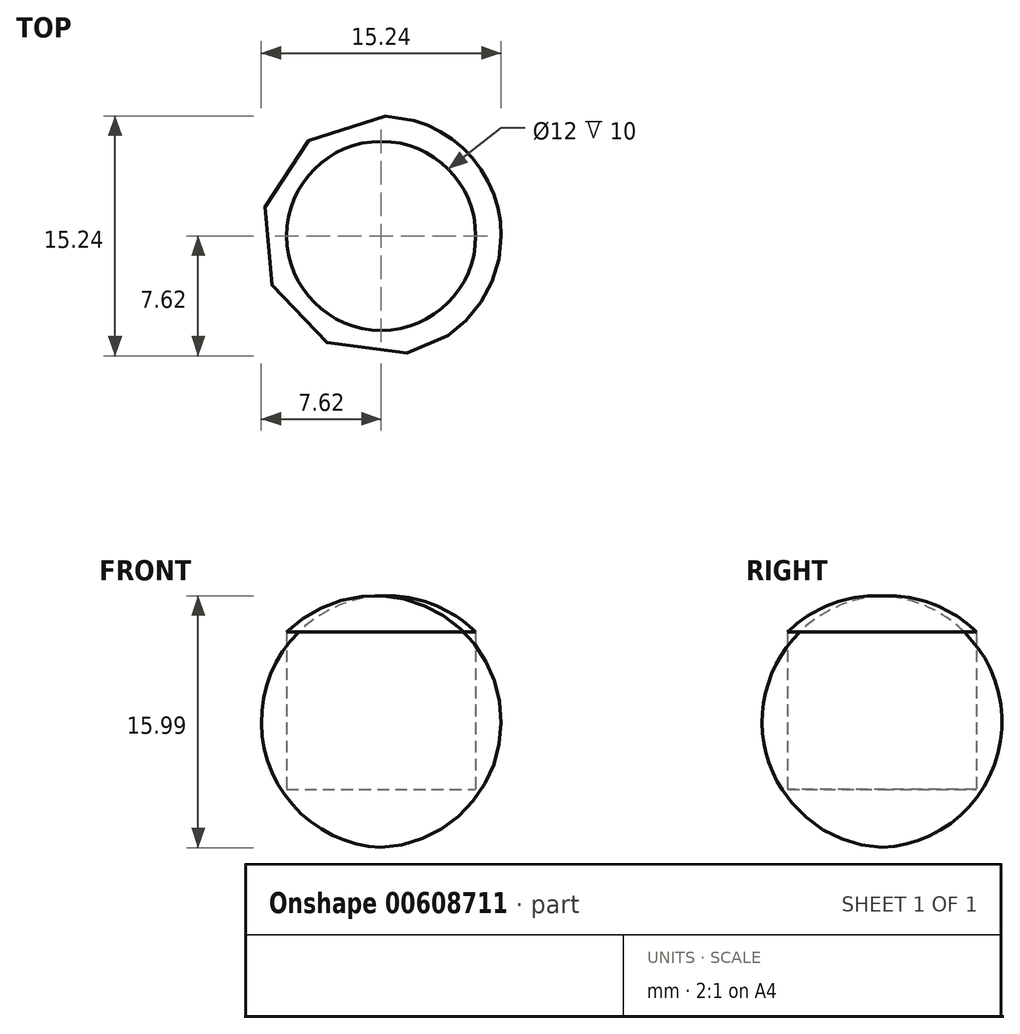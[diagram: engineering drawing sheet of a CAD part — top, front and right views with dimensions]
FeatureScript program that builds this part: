
annotation { "Feature Type Name" : "Feature", "Feature Type Description" : "" }
export const myFeature = defineFeature(function(context is Context, id is Id, definition is map)
    precondition{}
    {
        {
            var Q0;
            Q0=qCreatedBy(makeId("Front.planeOp"),FACE);
            var sketch = newSketch(context, id + "F0", { "sketchPlane" : qUnion([Q0])});
            skLineSegment(sketch, "E0", {"start": v(0, 0) * mm, "end": v(-6, 0) * mm});
            skLineSegment(sketch, "E1", {"start": v(0, 0) * mm, "end": v(0, 2.3) * mm});
            skArc(sketch, "E2", {"start": v(0, 2.3) * mm, "mid": v(-3.24, 1.78) * mm, "end": v(-6, 0) * mm});
            skSolve(sketch);
        }
        {
            var Q0;
            Q0=makeQuery(id+"F0.imprint","IMPRINT",FACE,{"disambiguationData":[TD([[makeQuery(id+"F0.imprint","IMPRINT",EDGE,{"derivedFrom":sQuery(id+"F0.wireOp",EDGE,"E0")}),-1.0]])]});
            var Q1;
            Q1=sQuery(id+"F0.wireOp",EDGE,"E1");
            revolve(context, id + "F1", {"entities" : qUnion([Q0]), "axis" : qUnion([Q1]), "revolveType" : RevolveType.FULL});
        }
        {
            var Q0;
            Q0=qCreatedBy(makeId("Front.planeOp"),FACE);
            var sketch = newSketch(context, id + "F2", { "sketchPlane" : qUnion([Q0])});
            skLineSegment(sketch, "E3.bottom", {"start": v(6, 0) * mm, "end": v(-6, 0) * mm});
            skLineSegment(sketch, "E3.top", {"start": v(6, -10) * mm, "end": v(-6, -10) * mm});
            skLineSegment(sketch, "E3.left", {"start": v(6, 0) * mm, "end": v(6, -10) * mm});
            skLineSegment(sketch, "E3.right", {"start": v(-6, 0) * mm, "end": v(-6, -10) * mm});
            skPoint(sketch, "E3.middle", {"position": v(0, -5) * mm});
            skLineSegment(sketch, "E4", {"start": v(0, -10) * mm, "end": v(0, 0) * mm});
            skSolve(sketch);
        }
        {
            var Q0;
            {var subQ0=sQuery(id+"F2.wireOp",EDGE,"E3.right");Q0=makeQuery(id+"F2.imprint","IMPRINT",FACE,{"disambiguationData":[TD([[makeQuery(id+"F2.imprint","IMPRINT",EDGE,{"derivedFrom":subQ0}),1.0]])]});}
            var Q1;
            Q1=sQuery(id+"F2.wireOp",EDGE,"E4");
            revolve(context, id + "F3", {"operationType" : NewBodyOperationType.ADD, "entities" : qUnion([Q0]), "axis" : qUnion([Q1]), "revolveType" : RevolveType.FULL});
        }
    });
